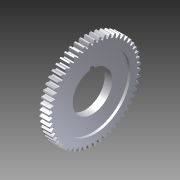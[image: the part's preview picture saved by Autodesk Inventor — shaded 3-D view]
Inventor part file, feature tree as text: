
AUTODESK INVENTOR PART (.ipt)
format: ipt  version: 2012 (Build 160160000, 160)  size: 1,039,360 bytes
history: native  units: in
note: dims shown in document units (in); Inventor stores cm internally (conversion verified against a paired STEP export)
features: extrude x2, sketch x1, imported_body x1
ambient origin geometry x8: Origin, YZ Plane, XZ Plane, XY Plane, X Axis, Y Axis, Z Axis, Center Point
feature tree (4):
  sketch  "Sketch1"  dims[d0=0.375in d3=0.3in d4=0.0in d5=1.0in d6=0.125in d7=0.125in d8=0.0625in d9=0.5625in d10=2.0in d11=1.0in d12=0.0in]
  extrude  "Extrusion2"  Depth=0.3in TaperAngle=0.0deg
  extrude  "Extrusion3"  Depth=1.0in
  imported_body  "Base1"
